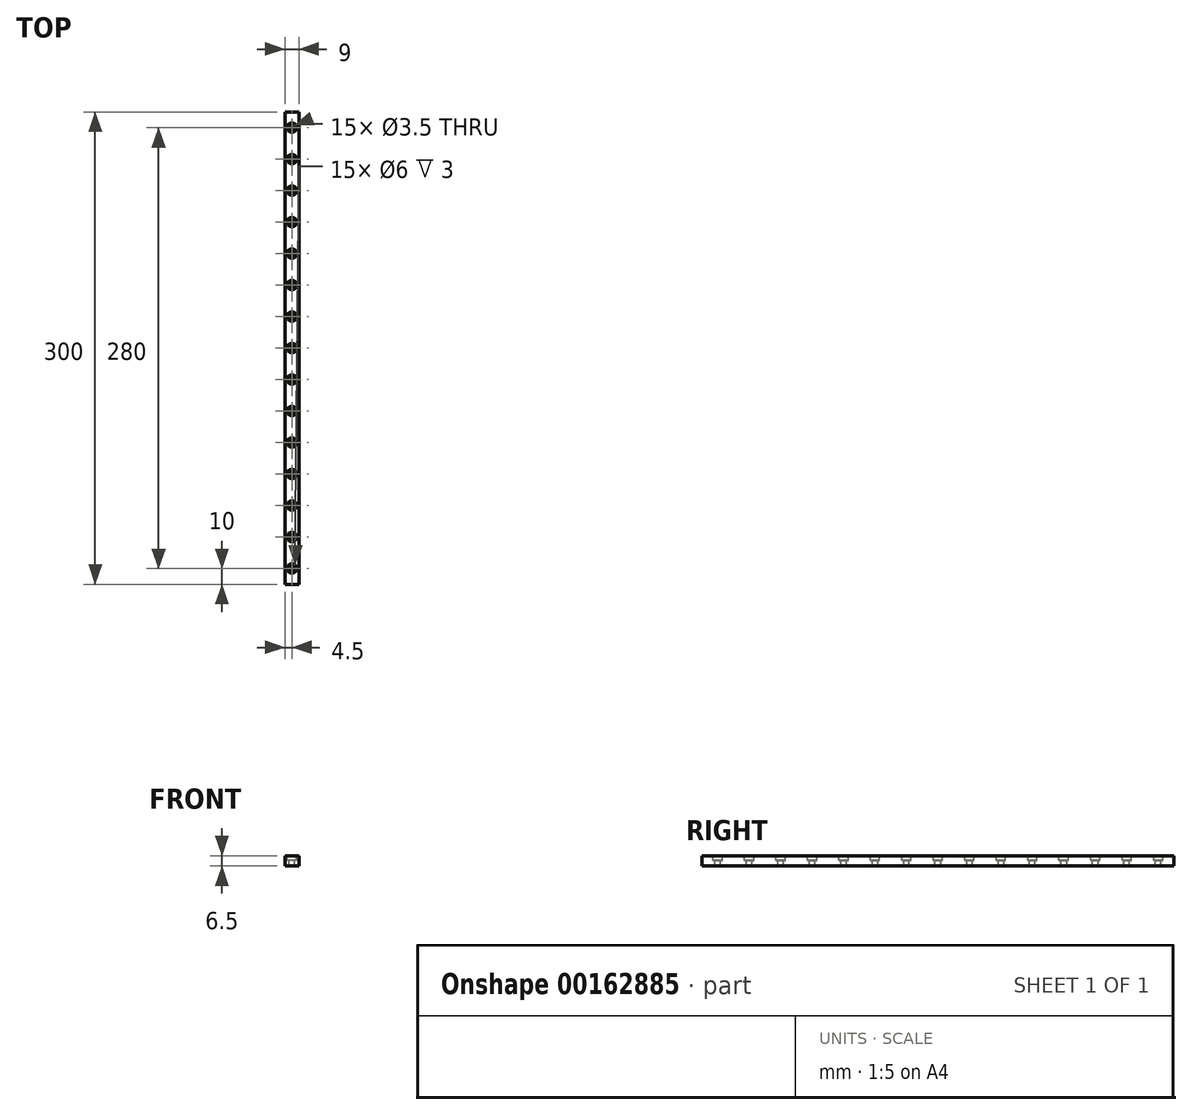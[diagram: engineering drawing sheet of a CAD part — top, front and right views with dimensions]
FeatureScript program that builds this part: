
annotation { "Feature Type Name" : "Feature", "Feature Type Description" : "" }
export const myFeature = defineFeature(function(context is Context, id is Id, definition is map)
    precondition{}
    {
        {
            var Q0;
            Q0=qCreatedBy(makeId("Front.planeOp"),FACE);
            var sketch = newSketch(context, id + "F0", { "sketchPlane" : qUnion([Q0])});
            skLineSegment(sketch, "E0.bottom", {"start": v(4.5, -3.25) * mm, "end": v(-4.5, -3.25) * mm});
            skLineSegment(sketch, "E0.top", {"start": v(4.5, 3.25) * mm, "end": v(-4.5, 3.25) * mm});
            skLineSegment(sketch, "E0.left", {"start": v(4.5, -3.25) * mm, "end": v(4.5, 3.25) * mm});
            skLineSegment(sketch, "E0.right", {"start": v(-4.5, -3.25) * mm, "end": v(-4.5, 3.25) * mm});
            skPoint(sketch, "E0.middle", {"position": v(0, 0) * mm});
            skSolve(sketch);
        }
        {
            var Q0;
            Q0=makeQuery(id+"F0.imprint","IMPRINT",FACE,{"disambiguationData":[TD([[makeQuery(id+"F0.imprint","IMPRINT",EDGE,{"derivedFrom":sQuery(id+"F0.wireOp",EDGE,"E0.bottom")}),-1.0]])]});
            extrude(context, id + "F1", {"entities" : qUnion([Q0]), "depth" : 150 * mm, "offsetDistance" : 25 * mm, "hasSecondDirection" : true, "secondDirectionOppositeDirection" : true, "secondDirectionDepth" : 150 * mm});
        }
        {
            var Q0;
            Q0=makeQuery(id+"F1.opExtrude","SWEPT_FACE",FACE,{"disambiguationData":[OSD([sQuery(id+"F0.wireOp",EDGE,"E0.top")])]});
            var sketch = newSketch(context, id + "F2", { "sketchPlane" : qUnion([Q0])});
            skPoint(sketch, "E1", {"position": v(0, -140) * mm});
            skPoint(sketch, "E2.0.1.0", {"position": v(0, -120) * mm});
            skPoint(sketch, "E2.0.2.0", {"position": v(0, -100) * mm});
            skPoint(sketch, "E2.0.3.0", {"position": v(0, -80) * mm});
            skPoint(sketch, "E2.0.4.0", {"position": v(0, -60) * mm});
            skPoint(sketch, "E2.0.5.0", {"position": v(0, -40) * mm});
            skPoint(sketch, "E2.0.6.0", {"position": v(0, -20) * mm});
            skPoint(sketch, "E2.0.7.0", {"position": v(0, 0) * mm});
            skPoint(sketch, "E2.0.8.0", {"position": v(0, 20) * mm});
            skPoint(sketch, "E2.0.9.0", {"position": v(0, 40) * mm});
            skPoint(sketch, "E2.0.10.0", {"position": v(0, 60) * mm});
            skPoint(sketch, "E2.0.11.0", {"position": v(0, 80) * mm});
            skLineSegment(sketch, "E2.direction1", {"start": v(0, -140) * mm, "end": v(25, -140) * mm, "construction": true});
            skLineSegment(sketch, "E2.direction2", {"start": v(0, -140) * mm, "end": v(0, -120) * mm, "construction": true});
            skPoint(sketch, "E3.0.0.12", {"position": v(0, 100) * mm});
            skPoint(sketch, "E3.0.0.13", {"position": v(0, 120) * mm});
            skPoint(sketch, "E3.0.0.14", {"position": v(0, 140) * mm});
            skSolve(sketch);
        }
        {
            var Q0;
            Q0=sQuery(id+"F2.wireOp",VERTEX,"E1");
            var Q1;
            Q1=sQuery(id+"F2.wireOp",VERTEX,"E2.0.1.0");
            var Q2;
            Q2=sQuery(id+"F2.wireOp",VERTEX,"E2.0.2.0");
            var Q3;
            Q3=sQuery(id+"F2.wireOp",VERTEX,"E2.0.3.0");
            var Q4;
            Q4=sQuery(id+"F2.wireOp",VERTEX,"E2.0.4.0");
            var Q5;
            Q5=sQuery(id+"F2.wireOp",VERTEX,"E2.0.5.0");
            var Q6;
            Q6=sQuery(id+"F2.wireOp",VERTEX,"E2.0.6.0");
            var Q7;
            Q7=sQuery(id+"F2.wireOp",VERTEX,"E2.0.7.0");
            var Q8;
            Q8=sQuery(id+"F2.wireOp",VERTEX,"E2.0.8.0");
            var Q9;
            Q9=sQuery(id+"F2.wireOp",VERTEX,"E2.0.9.0");
            var Q10;
            Q10=sQuery(id+"F2.wireOp",VERTEX,"E2.0.10.0");
            var Q11;
            Q11=sQuery(id+"F2.wireOp",VERTEX,"E2.0.11.0");
            var Q12;
            Q12=sQuery(id+"F2.wireOp",VERTEX,"E3.0.0.12");
            var Q13;
            Q13=sQuery(id+"F2.wireOp",VERTEX,"E3.0.0.13");
            var Q14;
            Q14=sQuery(id+"F2.wireOp",VERTEX,"E3.0.0.14");
            var Q15;
            Q15=makeQuery(id+"F1.opExtrude","SWEPT_BODY",BODY,{"disambiguationData":[OSD([sQuery(id+"F0.wireOp",EDGE,"E0.bottom"),sQuery(id+"F0.wireOp",EDGE,"E0.top"),sQuery(id+"F0.wireOp",EDGE,"E0.left"),sQuery(id+"F0.wireOp",EDGE,"E0.right")])]});
            hole(context, id + "F3", {"style" : HoleStyle.C_BORE, "endStyle" : HoleEndStyle.THROUGH, "holeDiameter" : 3.5 * mm, "cBoreDiameter" : 6 * mm, "cBoreDepth" : 3 * mm, "majorDiameter" : 5 * mm, "isTappedThrough" : true, "tappedDepth" : 12 * mm, "tapClearance" : 3, "startFromSketch" : true, "locations" : qUnion([Q0, Q1, Q2, Q3, Q4, Q5, Q6, Q7, Q8, Q9, Q10, Q11, Q12, Q13, Q14]), "scope" : qUnion([Q15])});
        }
    });
